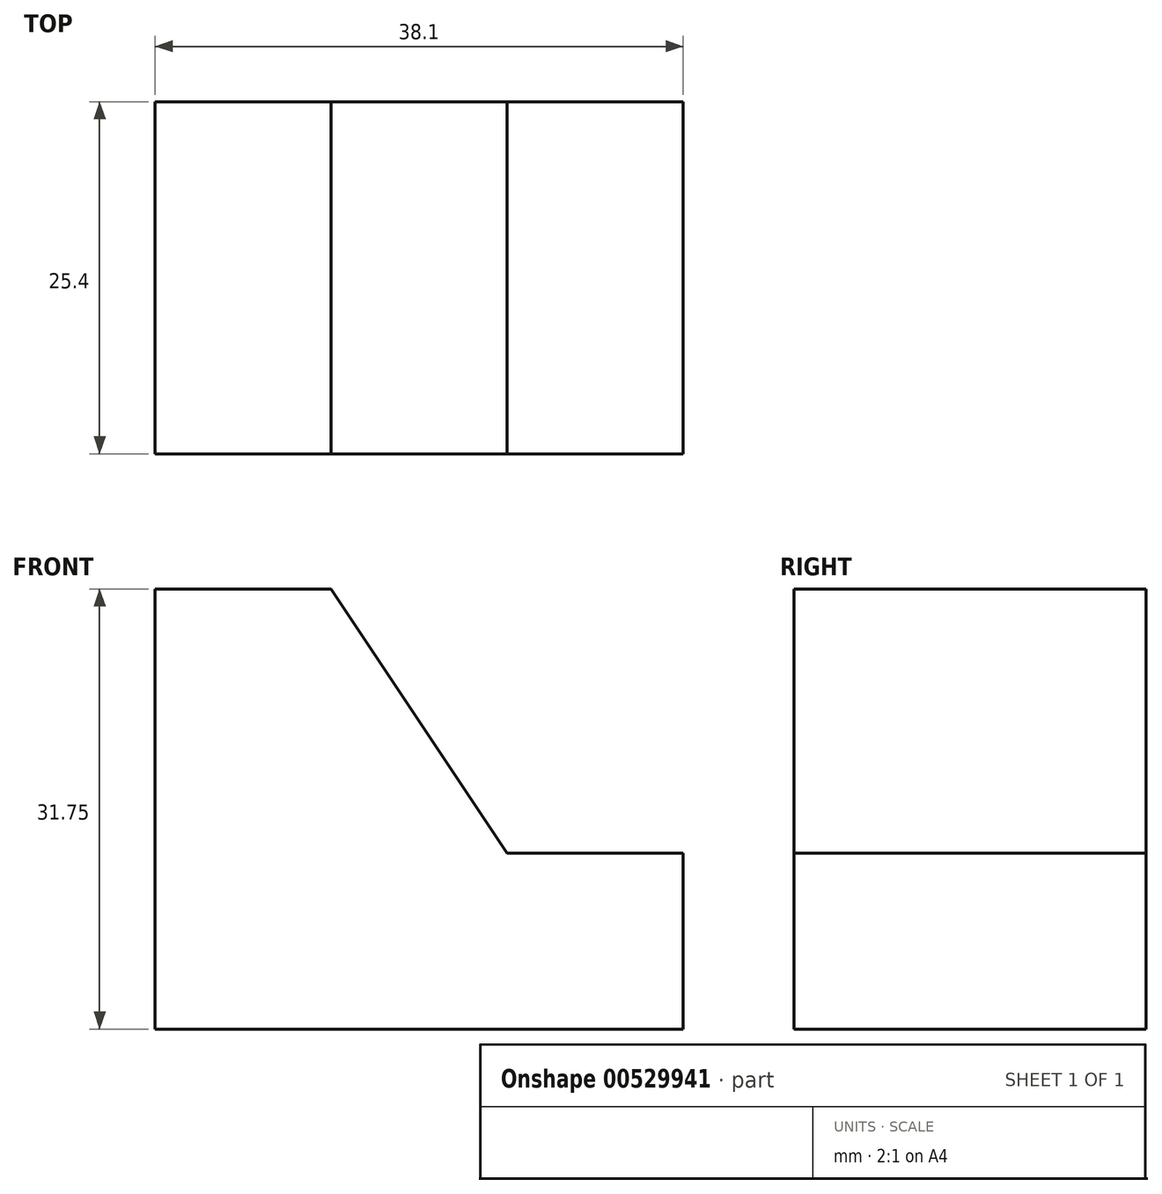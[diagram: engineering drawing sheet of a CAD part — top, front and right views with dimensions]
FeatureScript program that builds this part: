
annotation { "Feature Type Name" : "Feature", "Feature Type Description" : "" }
export const myFeature = defineFeature(function(context is Context, id is Id, definition is map)
    precondition{}
    {
        {
            var Q0;
            Q0=qCreatedBy(makeId("Front.planeOp"),FACE);
            var sketch = newSketch(context, id + "F0", { "sketchPlane" : qUnion([Q0])});
            skLineSegment(sketch, "E0", {"start": v(-12.38, 11.33) * mm, "end": v(-12.38, 24.03) * mm});
            skLineSegment(sketch, "E1", {"start": v(-12.38, 24.03) * mm, "end": v(-25.08, 24.03) * mm});
            skLineSegment(sketch, "E2", {"start": v(-12.38, 11.33) * mm, "end": v(-50.48, 11.33) * mm});
            skLineSegment(sketch, "E3", {"start": v(-50.48, 11.33) * mm, "end": v(-50.48, 43.08) * mm});
            skLineSegment(sketch, "E4", {"start": v(-50.48, 43.08) * mm, "end": v(-37.78, 43.08) * mm});
            skLineSegment(sketch, "E5", {"start": v(-37.78, 43.08) * mm, "end": v(-25.08, 24.03) * mm});
            skSolve(sketch);
        }
        {
            var Q0;
            Q0=makeQuery(id+"F0.imprint","IMPRINT",FACE,{"disambiguationData":[TD([[makeQuery(id+"F0.imprint","IMPRINT",EDGE,{"derivedFrom":sQuery(id+"F0.wireOp",EDGE,"E0")}),1.0]])]});
            extrude(context, id + "F1", {"entities" : qUnion([Q0]), "depth" : 25.4 * mm, "offsetDistance" : 25.4 * mm});
        }
    });
